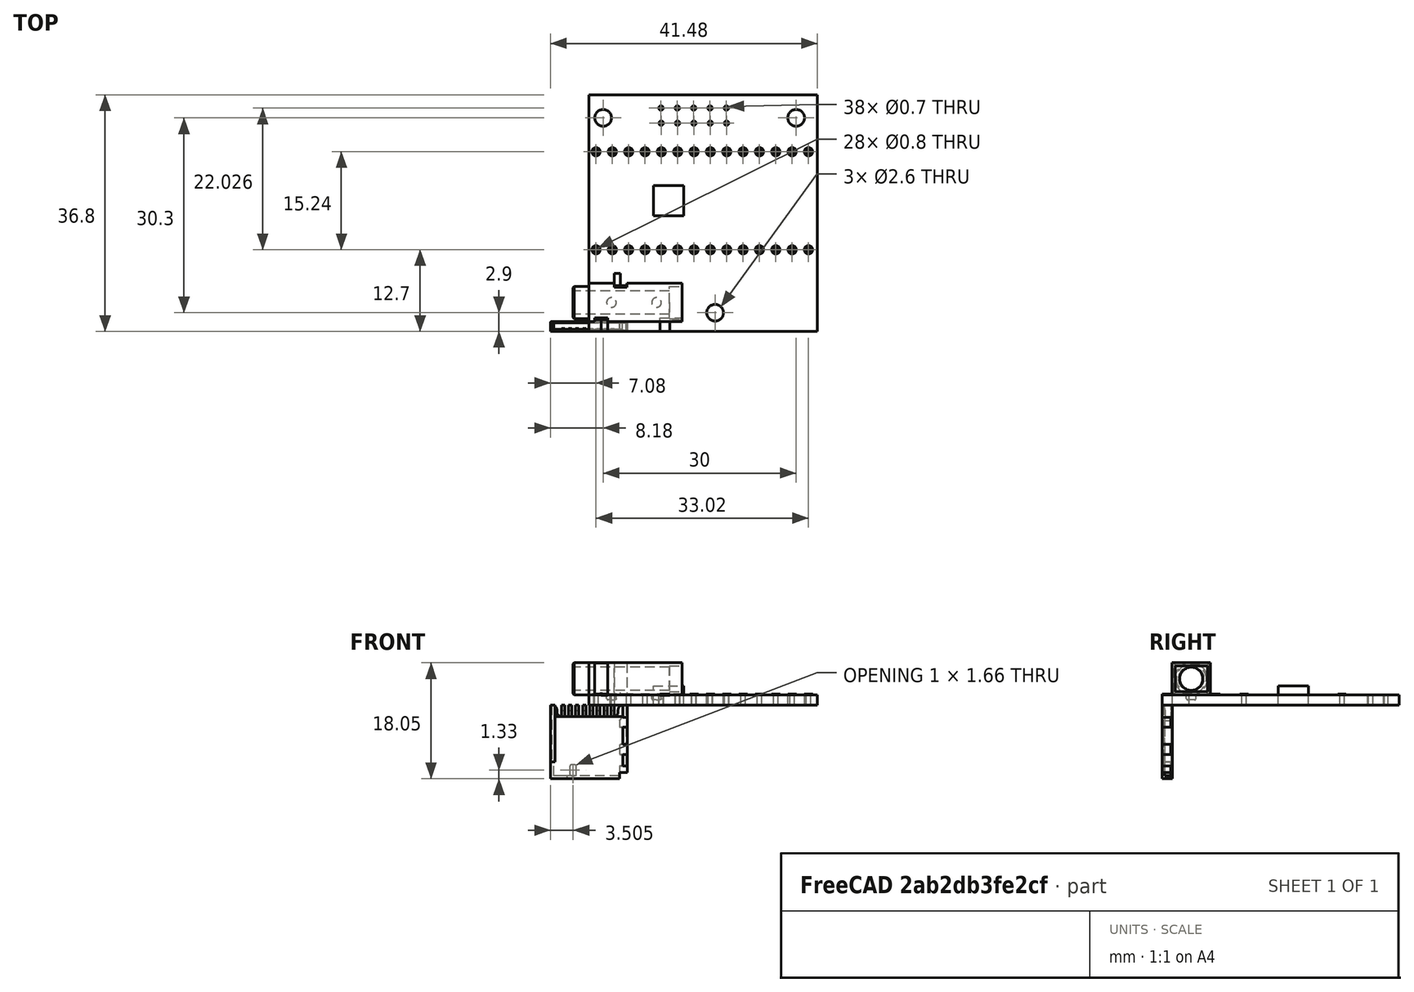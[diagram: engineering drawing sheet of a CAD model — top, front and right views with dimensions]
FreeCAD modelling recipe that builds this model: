
FCSTD DOCUMENT  (FreeCAD 0.18.4R)
Label: TeensyAudioBoard
License: All rights reserved
LicenseURL: http://en.wikipedia.org/wiki/All_rights_reserved
objects: Part::Cut×20, Part::Cylinder×19, Part::Feature×13, Part::FeaturePython×10, PartDesign::Body×8, Part::Compound×5, Part::Box×2, App::Part×2, Sketcher::SketchObject×1, App::DocumentObjectGroup×1
note: 78 computed .brp shape members not serialized (recipe doc carries the construction recipe); baked Part::Feature solids carry a one-line shape summary decoded from their .brp

FEATURE [Part::Feature] Part__Feature  label="Headphone jack"
  Placement = pos=(0,4.5,1.6) rot=(1,0,0;1.5708rad)
  shape: bbox 17 x 9 x 5.8 mm, 69 faces (baked)
FEATURE [Part::Box] Box  label="Cube"
  AttacherType = Attacher::AttachEngine3D
  Height = 1.6
  Length = 35.5
  Width = 36.8
FEATURE [Part::Cylinder] Cylinder
  Angle = 360
  AttacherType = Attacher::AttachEngine3D
  Height = 1.6
  Placement = pos=(19.6,2.9,0) rot=(0,0,1;0rad)
  Radius = 1.3
FEATURE [Part::Cut] Cut
  Base = -> Box
  Tool = -> Cylinder
FEATURE [Part::Cylinder] Cylinder001
  Angle = 360
  AttacherType = Attacher::AttachEngine3D
  Height = 1.6
  Placement = pos=(2.2,33.2,0) rot=(0,0,1;0rad)
  Radius = 1.3
FEATURE [Part::Cut] Cut001
  Base = -> Cut
  Tool = -> Cylinder001
FEATURE [Part::Cylinder] Cylinder002
  Angle = 360
  AttacherType = Attacher::AttachEngine3D
  Height = 1.6
  Placement = pos=(32.2,33.2,0) rot=(0,0,1;0rad)
  Radius = 1.3
FEATURE [Part::Cut] Cut002
  Base = -> Cut001
  Tool = -> Cylinder002
FEATURE [Part::Feature] Part__Feature043  label="Component047"
  shape: bbox 0.5 x 0.45 x 1.8 mm, 8 faces (baked)
FEATURE [Part::Feature] Part__Feature044  label="Component048"
  Placement = pos=(4.4,0,9e-15) rot=(0,0,1;0rad)
  shape: bbox 0.5 x 0.45 x 1.8 mm, 8 faces (baked)
FEATURE [Part::Feature] Part__Feature046  label="Component050"
  Placement = pos=(5.5,0,9e-15) rot=(0,0,1;0rad)
  shape: bbox 0.5 x 0.45 x 1.8 mm, 8 faces (baked)
FEATURE [Part::Feature] Part__Feature045  label="Component049"
  Placement = pos=(1.1,0,0) rot=(0,0,1;0rad)
  shape: bbox 0.5 x 0.45 x 1.8 mm, 8 faces (baked)
FEATURE [Part::Feature] Part__Feature047  label="Component051"
  Placement = pos=(6.6,0,0) rot=(0,0,1;0rad)
  shape: bbox 0.5 x 0.45 x 1.8 mm, 8 faces (baked)
FEATURE [Part::Feature] Part__Feature048  label="Component052"
  Placement = pos=(3.3,0,0) rot=(0,0,1;0rad)
  shape: bbox 0.5 x 0.45 x 1.8 mm, 8 faces (baked)
FEATURE [Part::Feature] Part__Feature049  label="Component053"
  Placement = pos=(2.2,0,0) rot=(0,0,1;0rad)
  shape: bbox 0.5 x 0.45 x 1.8 mm, 8 faces (baked)
FEATURE [Part::Feature] Part__Feature050  label="Case"
  shape: bbox 11.95 x 1.55 x 11.45 mm, 59 faces (baked)
FEATURE [Part::Feature] Part__Feature041  label="Base"
  shape: bbox 11.95 x 1.35 x 9.65 mm, 32 faces (baked)
FEATURE [Part::Feature] Part__Feature042  label="Component2"
  Placement = pos=(7.7,0,0) rot=(0,0,1;0rad)
  shape: bbox 0.5 x 0.45 x 1.8 mm, 8 faces (baked)
FEATURE [App::Part] Pins
  Group = -> [Part__Feature042,Part__Feature043,Part__Feature044,Part__Feature045,Part__Feature046,Part__Feature047,Part__Feature048,Part__Feature049]
  Origin = -> Origin006
FEATURE [PartDesign::Body] Body006
  Origin = -> Origin013
FEATURE [Part::Cylinder] Cylinder004
  Angle = 360
  AttacherType = Attacher::AttachEngine3D
  Height = 1.6
  Placement = pos=(3.64,12.7,0) rot=(0,0,1;0rad)
  Radius = 0.35
FEATURE [Part::Cylinder] Cylinder006
  Angle = 360
  AttacherType = Attacher::AttachEngine3D
  Height = 0.1
  Placement = pos=(0,0,1.62) rot=(0,0,1;0rad)
  Radius = 0.65
FEATURE [Part::Cylinder] Cylinder007
  Angle = 360
  AttacherType = Attacher::AttachEngine3D
  Height = 0.1
  Placement = pos=(0,0,1.62) rot=(0,0,1;0rad)
  Radius = 0.4
FEATURE [Part::Cut] Cut003
  Base = -> Cylinder006
  Placement = pos=(1.1,12.7,0) rot=(0,0,1;0rad)
  Tool = -> Cylinder007
FEATURE [Part::Cylinder] Cylinder008
  Angle = 360
  AttacherType = Attacher::AttachEngine3D
  Height = 1.6
  Placement = pos=(1.1,12.7,0) rot=(0,0,1;0rad)
  Radius = 0.35
FEATURE [Part::Cylinder] Cylinder009
  Angle = 360
  AttacherType = Attacher::AttachEngine3D
  Height = 1.6
  Placement = pos=(8.72,12.7,0) rot=(0,0,1;0rad)
  Radius = 0.35
FEATURE [Part::Cylinder] Cylinder010
  Angle = 360
  AttacherType = Attacher::AttachEngine3D
  Height = 1.6
  Placement = pos=(6.18,12.7,0) rot=(0,0,1;0rad)
  Radius = 0.35
FEATURE [Part::Cylinder] Cylinder011
  Angle = 360
  AttacherType = Attacher::AttachEngine3D
  Height = 1.6
  Placement = pos=(11.26,12.7,0) rot=(0,0,1;0rad)
  Radius = 0.35
FEATURE [Part::Cylinder] Cylinder012
  Angle = 360
  AttacherType = Attacher::AttachEngine3D
  Height = 1.6
  Placement = pos=(13.8,12.7,0) rot=(0,0,1;0rad)
  Radius = 0.35
FEATURE [Part::Cylinder] Cylinder013
  Angle = 360
  AttacherType = Attacher::AttachEngine3D
  Height = 1.6
  Placement = pos=(18.88,12.7,0) rot=(0,0,1;0rad)
  Radius = 0.35
FEATURE [Part::Cylinder] Cylinder014
  Angle = 360
  AttacherType = Attacher::AttachEngine3D
  Height = 1.6
  Placement = pos=(23.96,12.7,0) rot=(0,0,1;0rad)
  Radius = 0.35
FEATURE [Part::Cylinder] Cylinder015
  Angle = 360
  AttacherType = Attacher::AttachEngine3D
  Height = 1.6
  Placement = pos=(21.42,12.7,0) rot=(0,0,1;0rad)
  Radius = 0.35
FEATURE [Part::Cylinder] Cylinder016
  Angle = 360
  AttacherType = Attacher::AttachEngine3D
  Height = 1.6
  Placement = pos=(16.34,12.7,0) rot=(0,0,1;0rad)
  Radius = 0.35
FEATURE [Part::Cylinder] Cylinder017
  Angle = 360
  AttacherType = Attacher::AttachEngine3D
  Height = 1.6
  Placement = pos=(29.04,12.7,0) rot=(0,0,1;0rad)
  Radius = 0.35
FEATURE [Part::Cylinder] Cylinder018
  Angle = 360
  AttacherType = Attacher::AttachEngine3D
  Height = 1.6
  Placement = pos=(34.12,12.7,0) rot=(0,0,1;0rad)
  Radius = 0.35
FEATURE [Part::Cylinder] Cylinder019
  Angle = 360
  AttacherType = Attacher::AttachEngine3D
  Height = 1.6
  Placement = pos=(31.58,12.7,0) rot=(0,0,1;0rad)
  Radius = 0.35
FEATURE [Part::Cylinder] Cylinder020
  Angle = 360
  AttacherType = Attacher::AttachEngine3D
  Height = 1.6
  Placement = pos=(26.5,12.7,0) rot=(0,0,1;0rad)
  Radius = 0.35
FEATURE [Part::Compound] Compound
  Links = -> [Cylinder004,Cylinder008,Cylinder009,Cylinder013,Cylinder018,Cylinder012,Cylinder015,Cylinder014,Cylinder016,Cylinder011,Cylinder010,Cylinder019,Cylinder020,Cylinder017]
FEATURE [Part::Compound] Compound001
  Links = -> [Cylinder004,Cylinder008,Cylinder009,Cylinder013,Cylinder018,Cylinder012,Cylinder015,Cylinder014,Cylinder016,Cylinder011,Cylinder010,Cylinder019,Cylinder020,Cylinder017]
  Placement = pos=(0,15.24,0) rot=(0,0,1;0rad)
FEATURE [Part::Cut] Cut004
  Base = -> Cut002
  Tool = -> Compound
FEATURE [Part::Cut] Cut005  label="main board"
  Base = -> Cut004
  Tool = -> Compound001
FEATURE [Part::Cut] Cut006
  Base = -> Cylinder006
  Placement = pos=(3.64,12.7,0) rot=(0,0,1;0rad)
  Tool = -> Cylinder007
FEATURE [Part::Cut] Cut008
  Base = -> Cylinder006
  Placement = pos=(8.72,12.7,0) rot=(0,0,1;0rad)
  Tool = -> Cylinder007
FEATURE [Part::Cut] Cut009
  Base = -> Cylinder006
  Placement = pos=(11.26,12.7,0) rot=(0,0,1;0rad)
  Tool = -> Cylinder007
FEATURE [Part::Cut] Cut010
  Base = -> Cylinder006
  Placement = pos=(13.8,12.7,0) rot=(0,0,1;0rad)
  Tool = -> Cylinder007
FEATURE [Part::Cut] Cut012
  Base = -> Cylinder006
  Placement = pos=(18.88,12.7,0) rot=(0,0,1;0rad)
  Tool = -> Cylinder007
FEATURE [Part::Cut] Cut013
  Base = -> Cylinder006
  Placement = pos=(21.42,12.7,0) rot=(0,0,1;0rad)
  Tool = -> Cylinder007
FEATURE [Part::Cut] Cut014
  Base = -> Cylinder006
  Placement = pos=(23.96,12.7,0) rot=(0,0,1;0rad)
  Tool = -> Cylinder007
FEATURE [Part::Cut] Cut015
  Base = -> Cylinder006
  Placement = pos=(26.5,12.7,0) rot=(0,0,1;0rad)
  Tool = -> Cylinder007
FEATURE [Part::Cut] Cut016
  Base = -> Cylinder006
  Placement = pos=(29.04,12.7,0) rot=(0,0,1;0rad)
  Tool = -> Cylinder007
FEATURE [Part::Cut] Cut017
  Base = -> Cylinder006
  Placement = pos=(31.58,12.7,0) rot=(0,0,1;0rad)
  Tool = -> Cylinder007
FEATURE [Part::Cut] Cut018
  Base = -> Cylinder006
  Placement = pos=(34.12,12.7,0) rot=(0,0,1;0rad)
  Tool = -> Cylinder007
FEATURE [Part::Cut] Cut011
  Base = -> Cylinder006
  Placement = pos=(16.34,12.7,0) rot=(0,0,1;0rad)
  Tool = -> Cylinder007
FEATURE [Part::Cut] Cut007
  Base = -> Cylinder006
  Placement = pos=(6.18,12.7,0) rot=(0,0,1;0rad)
  Tool = -> Cylinder007
FEATURE [Part::Compound] Compound002  label="Teensy pins left"
  Links = -> [Cut003,Cut006,Cut018,Cut010,Cut016,Cut013,Cut011,Cut012,Cut017,Cut008,Cut015,Cut009,Cut014,Cut007]
FEATURE [Part::Compound] Compound003  label="Teensy pins right"
  Links = -> [Cut003,Cut006,Cut018,Cut010,Cut016,Cut013,Cut011,Cut012,Cut017,Cut008,Cut015,Cut009,Cut014,Cut007]
  Placement = pos=(0,15.24,0) rot=(0,0,1;0rad)
FEATURE [Part::Box] Box001  label="2"
  AttacherType = Attacher::AttachEngine3D
  Height = 3
  Length = 4.7
  Placement = pos=(10,18,0) rot=(0,0,1;0rad)
  Width = 4.7
FEATURE [Part::Feature] Cylinder021_fd_cp  label="Cylinder021_sp"
  Placement = pos=(11.0785,24.613,0) rot=(0,0,1;0rad)
  shape: bbox 33.72 x 0.7 x 1.6 mm, 42 faces, 14 solids (baked)
FEATURE [PartDesign::Body] Body
  Origin = -> Origin
FEATURE [PartDesign::Body] Body001
  Origin = -> Origin008
FEATURE [PartDesign::Body] Body002
  Origin = -> Origin009
FEATURE [PartDesign::Body] Body003
  Origin = -> Origin010
FEATURE [PartDesign::Body] Body004
  Origin = -> Origin011
FEATURE [PartDesign::Body] Body005
  Origin = -> Origin012
FEATURE [Sketcher::SketchObject] Sketch
  MapMode = 5
  Support = -> [XY_Plane014]
FEATURE [PartDesign::Body] Body007
  Group = -> [Sketch]
  Origin = -> Origin014
FEATURE [App::Part] HR5_DM3D_Micro_SD_Card_v4  label="SD Card"
  Group = -> [Part__Feature041,Pins,Part__Feature050,Body,Body001,Body002,Body003,Body004,Body005,Body006,Body007]
  Origin = -> Origin007
  Placement = pos=(35.5,20.5,1.6) rot=(0.57735,0.57735,0.57735;2.0944rad)
FEATURE [Part::Feature] Cylinder021_fd_cp001  label="Cylinder021_sp001"
  Placement = pos=(11.0785,24.613,0) rot=(0,0,1;0rad)
  shape: bbox 33.72 x 0.7 x 1.6 mm, 42 faces, 14 solids (baked)
FEATURE [Part::FeaturePython] Cylinder021_fd_cp_child005  label="Cylinder021_sp.005"  # WARN: FeaturePython — macro-defined, semantics opaque (R4)
  Base = -> Cylinder021_fd_cp001
  FilterType = 1
  Invert = false
  OverrideMaxVal = 0
  Placement = pos=(-1.12894,-2.23907,0) rot=(0,0,1;0rad)
  WindowFrom = 80
  WindowTo = 100
  items = 0
FEATURE [Part::FeaturePython] Cylinder021_fd_cp_child006  label="Cylinder021_sp.006"  # WARN: FeaturePython — macro-defined, semantics opaque (R4)
  Base = -> Cylinder021_fd_cp001
  FilterType = 1
  Invert = false
  OverrideMaxVal = 0
  Placement = pos=(-1.12894,-2.23907,0) rot=(0,0,1;0rad)
  WindowFrom = 80
  WindowTo = 100
  items = 4
FEATURE [Part::FeaturePython] Cylinder021_fd_cp_child007  label="Cylinder021_sp.007"  # WARN: FeaturePython — macro-defined, semantics opaque (R4)
  Base = -> Cylinder021_fd_cp001
  FilterType = 1
  Invert = false
  OverrideMaxVal = 0
  Placement = pos=(-1.12894,-2.23907,0) rot=(0,0,1;0rad)
  WindowFrom = 80
  WindowTo = 100
  items = 3
FEATURE [Part::FeaturePython] Cylinder021_fd_cp_child008  label="Cylinder021_sp.008"  # WARN: FeaturePython — macro-defined, semantics opaque (R4)
  Base = -> Cylinder021_fd_cp001
  FilterType = 1
  Invert = false
  OverrideMaxVal = 0
  Placement = pos=(-1.12894,-2.23907,0) rot=(0,0,1;0rad)
  WindowFrom = 80
  WindowTo = 100
  items = 2
FEATURE [Part::FeaturePython] Cylinder021_fd_cp_child009  label="Cylinder021_sp.009"  # WARN: FeaturePython — macro-defined, semantics opaque (R4)
  Base = -> Cylinder021_fd_cp001
  FilterType = 1
  Invert = false
  OverrideMaxVal = 0
  Placement = pos=(-1.12894,-2.23907,0) rot=(0,0,1;0rad)
  WindowFrom = 80
  WindowTo = 100
  items = 1
FEATURE [Part::FeaturePython] Cylinder021_fd_cp_child0  label="Cylinder021_sp.0"  # WARN: FeaturePython — macro-defined, semantics opaque (R4)
  Base = -> Cylinder021_fd_cp
  FilterType = 1
  Invert = false
  OverrideMaxVal = 0
  Placement = pos=(-1.15595,0.105087,0) rot=(0,0,1;0rad)
  WindowFrom = 80
  WindowTo = 100
  items = 0
FEATURE [Part::FeaturePython] Cylinder021_fd_cp_child1  label="Cylinder021_sp.1"  # WARN: FeaturePython — macro-defined, semantics opaque (R4)
  Base = -> Cylinder021_fd_cp
  FilterType = 1
  Invert = false
  OverrideMaxVal = 0
  Placement = pos=(-1.15595,0.105087,0) rot=(0,0,1;0rad)
  WindowFrom = 80
  WindowTo = 100
  items = 1
FEATURE [Part::FeaturePython] Cylinder021_fd_cp_child2  label="Cylinder021_sp.2"  # WARN: FeaturePython — macro-defined, semantics opaque (R4)
  Base = -> Cylinder021_fd_cp
  FilterType = 1
  Invert = false
  OverrideMaxVal = 0
  Placement = pos=(-1.15595,0.105087,0) rot=(0,0,1;0rad)
  WindowFrom = 80
  WindowTo = 100
  items = 2
FEATURE [Part::FeaturePython] Cylinder021_fd_cp_child3  label="Cylinder021_sp.3"  # WARN: FeaturePython — macro-defined, semantics opaque (R4)
  Base = -> Cylinder021_fd_cp
  FilterType = 1
  Invert = false
  OverrideMaxVal = 0
  Placement = pos=(-1.15595,0.105087,0) rot=(0,0,1;0rad)
  WindowFrom = 80
  WindowTo = 100
  items = 3
FEATURE [Part::FeaturePython] Cylinder021_fd_cp_child4  label="Cylinder021_sp.4"  # WARN: FeaturePython — macro-defined, semantics opaque (R4)
  Base = -> Cylinder021_fd_cp
  FilterType = 1
  Invert = false
  OverrideMaxVal = 0
  Placement = pos=(-1.15595,0.105087,0) rot=(0,0,1;0rad)
  WindowFrom = 80
  WindowTo = 100
  items = 4
FEATURE [Part::Compound] Compound004  label="Audio header"
  Links = -> [Cylinder021_fd_cp_child0,Cylinder021_fd_cp_child4,Cylinder021_fd_cp_child3,Cylinder021_fd_cp_child2,Cylinder021_fd_cp_child1,Cylinder021_fd_cp_child007,Cylinder021_fd_cp_child008,Cylinder021_fd_cp_child009,Cylinder021_fd_cp_child005,Cylinder021_fd_cp_child006]
FEATURE [App::DocumentObjectGroup] GrExplode_Cylinder021_fd_cp  label="Exploded Cylinder021_sp"
  Group = -> [Cylinder021_fd_cp_child0,Cylinder021_fd_cp_child1,Cylinder021_fd_cp_child2,Cylinder021_fd_cp_child3,Cylinder021_fd_cp_child4]
FEATURE [Part::Cut] Cut019
  Base = -> Cut005
  Tool = -> Compound004
